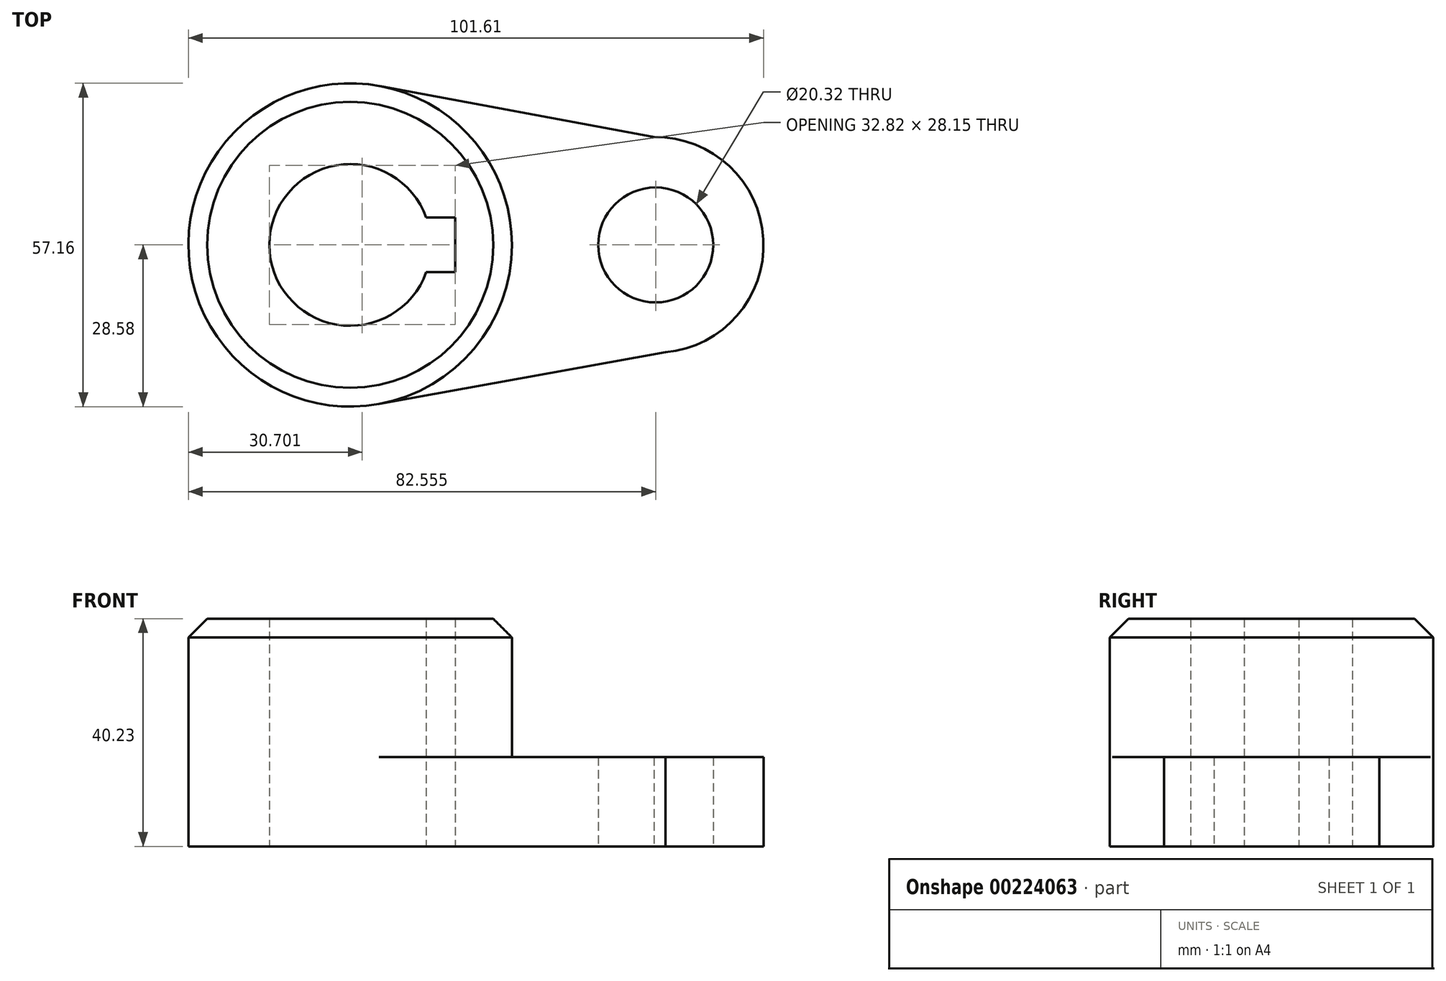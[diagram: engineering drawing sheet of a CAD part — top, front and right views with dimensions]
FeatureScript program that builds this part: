
annotation { "Feature Type Name" : "Feature", "Feature Type Description" : "" }
export const myFeature = defineFeature(function(context is Context, id is Id, definition is map)
    precondition{}
    {
        {
            var Q0;
            Q0=qCreatedBy(makeId("Top.planeOp"),FACE);
            var sketch = newSketch(context, id + "F0", { "sketchPlane" : qUnion([Q0])});
            skCircle(sketch, "E0", {"center": v(0, 0) * mm, "radius": 28.58 * mm});
            skCircle(sketch, "E1", {"center": v(0, 0) * mm, "radius": 14.29 * mm});
            skCircle(sketch, "E2", {"center": v(53.98, 0) * mm, "radius": 10.16 * mm});
            skCircle(sketch, "E3", {"center": v(53.98, 0) * mm, "radius": 19.05 * mm});
            skLineSegment(sketch, "E4", {"start": v(-14.29, 0) * mm, "end": v(18.53, 0) * mm, "construction": true});
            skLineSegment(sketch, "E5", {"start": v(18.53, 0) * mm, "end": v(18.53, 4.83) * mm});
            skLineSegment(sketch, "E6", {"start": v(18.53, 0) * mm, "end": v(18.53, -4.83) * mm});
            skLineSegment(sketch, "E7", {"start": v(18.53, 4.83) * mm, "end": v(13.45, 4.83) * mm});
            skLineSegment(sketch, "E8", {"start": v(18.53, -4.83) * mm, "end": v(13.45, -4.83) * mm});
            skLineSegment(sketch, "E9", {"start": v(53.69, 19.05) * mm, "end": v(5.24, 28.09) * mm});
            skLineSegment(sketch, "E10", {"start": v(55.68, -18.97) * mm, "end": v(5.08, -28.12) * mm});
            skSolve(sketch);
        }
        {
            var Q0;
            {var subQ0=sQuery(id+"F0.wireOp",EDGE,"acRxujln-zRDe-Jx8y-lfHx-LUMD3hYuCvqD");var subQ1=sQuery(id+"F0.wireOp",EDGE,"E0");var subQ2=makeQuery(id+"F0.imprint","INTERSECT",VERTEX,{"disambiguationData":[OD(1.0)],"derivedFrom":[subQ1,subQ0]});Q0=makeQuery(id+"F0.imprint","IMPRINT",FACE,{"disambiguationData":[TD([[makeQuery(id+"F0.imprint","IMPRINT",EDGE,{"disambiguationData":[TD([[subQ2,1.0]])],"derivedFrom":subQ1}),-1.0]])]});}
            var Q1;
            Q1=makeQuery(id+"F0.imprint","IMPRINT",FACE,{"disambiguationData":[TD([[makeQuery(id+"F0.imprint","IMPRINT",EDGE,{"derivedFrom":sQuery(id+"F0.wireOp",EDGE,"E2")}),-1.0]])]});
            extrude(context, id + "F1", {"entities" : qUnion([Q0, Q1]), "depth" : 15.77 * mm});
        }
        {
            var Q0;
            Q0=makeQuery(id+"F0.imprint","IMPRINT",FACE,{"disambiguationData":[TD([[makeQuery(id+"F0.imprint","IMPRINT",EDGE,{"derivedFrom":sQuery(id+"F0.wireOp",EDGE,"E5")}),-1.0]])]});
            extrude(context, id + "F2", {"entities" : qUnion([Q0]), "operationType" : NewBodyOperationType.ADD, "depth" : 40.23 * mm});
        }
        {
            var Q0;
            {var subQ0=sQuery(id+"F0.wireOp",EDGE,"E0");Q0=makeQuery(id+"F2.opExtrude","CAP_EDGE",EDGE,{"disambiguationData":[OSD([subQ0]),TDD([makeQuery(id+"F0.imprint","IMPRINT",EDGE,{"disambiguationData":[TD([[makeQuery(id+"F0.imprint","INTERSECT",VERTEX,{"disambiguationData":[OD(1.0)],"derivedFrom":[subQ0,sQuery(id+"F0.wireOp",EDGE,"acRxujln-zRDe-Jx8y-lfHx-LUMD3hYuCvqD")]}),1.0]])],"derivedFrom":subQ0})])],"isStart":false});}
            chamfer(context, id + "F3", {"entities" : qUnion([Q0]), "width" : 3.3 * mm, "tangentPropagation" : true});
        }
    });
